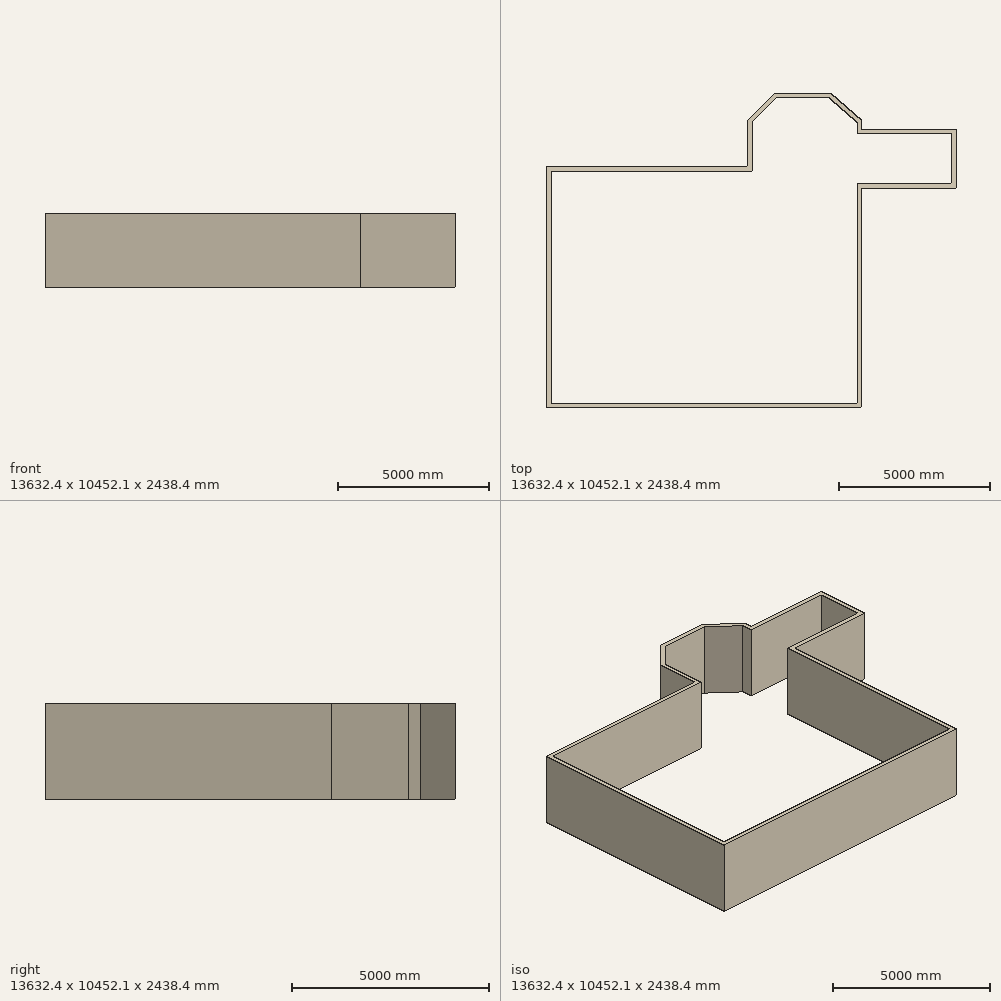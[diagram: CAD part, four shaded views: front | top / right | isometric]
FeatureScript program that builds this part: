
annotation { "Feature Type Name" : "Feature", "Feature Type Description" : "" }
export const myFeature = defineFeature(function(context is Context, id is Id, definition is map)
    precondition{}
    {
        {
            var Q0;
            Q0=qCreatedBy(makeId("Top.planeOp"),FACE);
            var sketch = newSketch(context, id + "F0", { "sketchPlane" : qUnion([Q0])});
            skLineSegment(sketch, "E0.bottom", {"start": v(0, 0) * mm, "end": v(10172.7, 0) * mm});
            skLineSegment(sketch, "E0.top", {"start": v(0, 7715.25) * mm, "end": v(6685.5, 7715.25) * mm});
            skLineSegment(sketch, "E0.left", {"start": v(0, 0) * mm, "end": v(0, 7715.25) * mm});
            skLineSegment(sketch, "E0.right", {"start": v(10172.7, 0) * mm, "end": v(10172.7, 7302.5) * mm});
            skLineSegment(sketch, "E1", {"start": v(10172.7, 7302.5) * mm, "end": v(13327.6, 7302.5) * mm});
            skLineSegment(sketch, "E2", {"start": v(13327.6, 7302.5) * mm, "end": v(13327.6, 8953.5) * mm});
            skLineSegment(sketch, "E3", {"start": v(13327.6, 8953.5) * mm, "end": v(10172.7, 8953.5) * mm});
            skLineSegment(sketch, "E4", {"start": v(6685.5, 7715.25) * mm, "end": v(6685.5, 9334.5) * mm});
            skLineSegment(sketch, "E5", {"start": v(6685.5, 9334.5) * mm, "end": v(7507.1, 10147.3) * mm});
            skLineSegment(sketch, "E6", {"start": v(7507.1, 10147.3) * mm, "end": v(9247, 10147.3) * mm});
            skLineSegment(sketch, "E7", {"start": v(9247, 10147.3) * mm, "end": v(10172.7, 9334.5) * mm});
            skLineSegment(sketch, "E8", {"start": v(10172.7, 9334.5) * mm, "end": v(10172.7, 8953.5) * mm});
            skLineSegment(sketch, "E9.0", {"start": v(13480, 7150.1) * mm, "end": v(13480, 9105.9) * mm});
            skLineSegment(sketch, "E9.1", {"start": v(6533.1, 9398.1) * mm, "end": v(7444.45, 10299.7) * mm});
            skLineSegment(sketch, "E9.2", {"start": v(7444.45, 10299.7) * mm, "end": v(9304.4, 10299.7) * mm});
            skLineSegment(sketch, "E9.3", {"start": v(9304.4, 10299.7) * mm, "end": v(10325.1, 9403.5) * mm});
            skLineSegment(sketch, "E9.4", {"start": v(10325.1, 9403.5) * mm, "end": v(10325.1, 9105.9) * mm});
            skLineSegment(sketch, "E9.5", {"start": v(6533.1, 7867.65) * mm, "end": v(6533.1, 9398.1) * mm});
            skLineSegment(sketch, "E9.6", {"start": v(13480, 9105.9) * mm, "end": v(10325.1, 9105.9) * mm});
            skLineSegment(sketch, "E9.7", {"start": v(-152.4, 7867.65) * mm, "end": v(6533.1, 7867.65) * mm});
            skLineSegment(sketch, "E9.8", {"start": v(-152.4, -152.4) * mm, "end": v(-152.4, 7867.65) * mm});
            skLineSegment(sketch, "E9.9", {"start": v(-152.4, -152.4) * mm, "end": v(10325.1, -152.4) * mm});
            skLineSegment(sketch, "E9.10", {"start": v(10325.1, -152.4) * mm, "end": v(10325.1, 7150.1) * mm});
            skLineSegment(sketch, "E9.11", {"start": v(10325.1, 7150.1) * mm, "end": v(13480, 7150.1) * mm});
            skSolve(sketch);
        }
        {
            var Q0;
            Q0 = qSketchRegion(id + "F0", true);
            extrude(context, id + "F1", {"entities" : qUnion([Q0]), "depth" : 2438.4 * mm});
        }
    });
